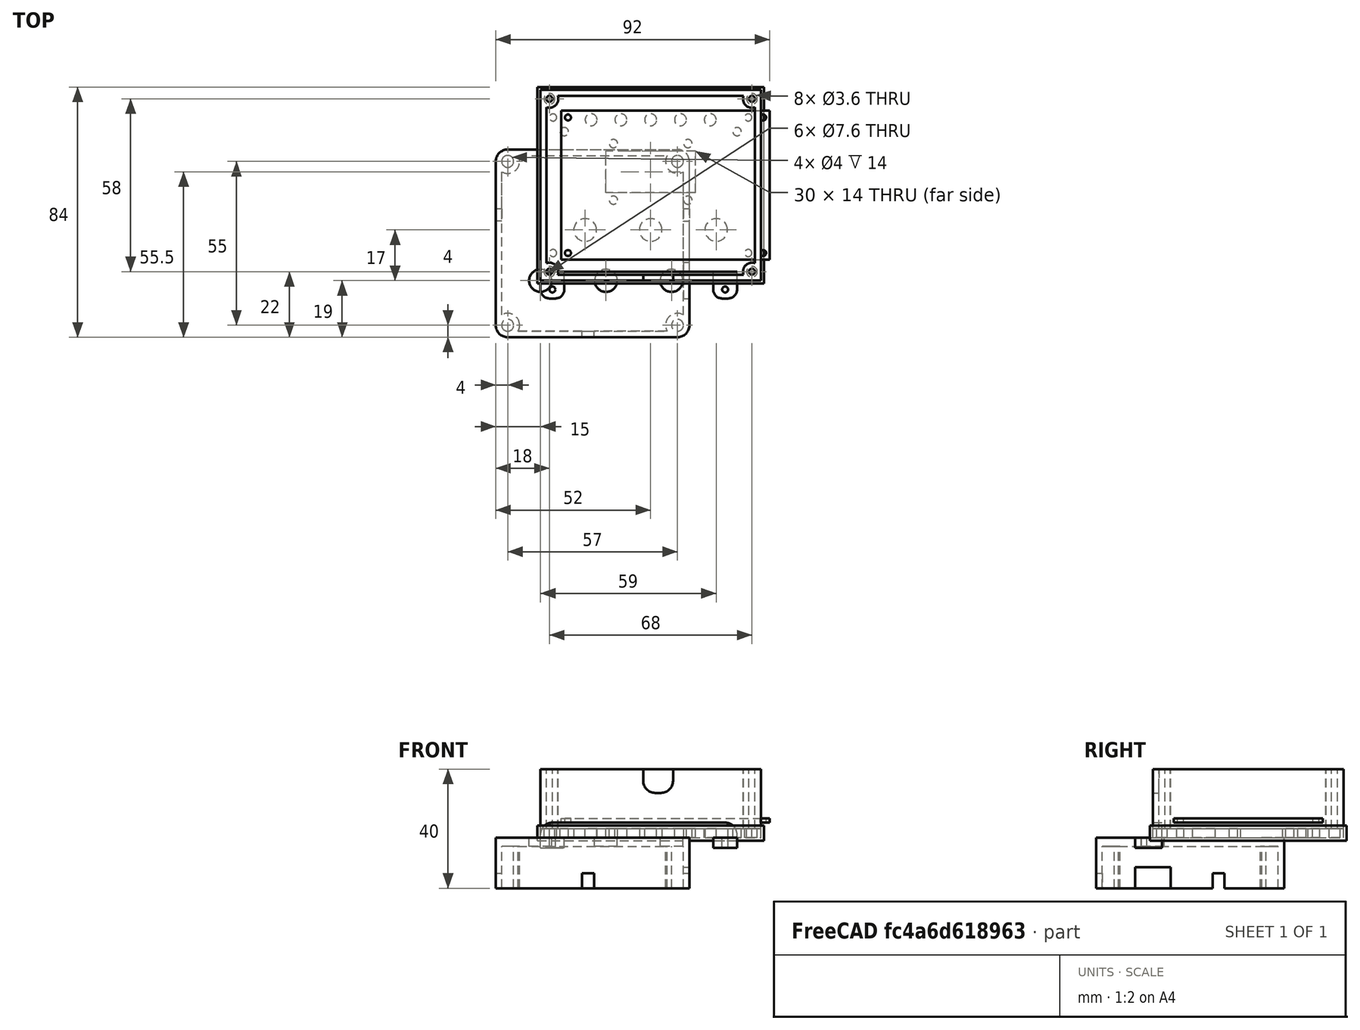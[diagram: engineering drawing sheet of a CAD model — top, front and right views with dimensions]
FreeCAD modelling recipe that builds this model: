
FCSTD DOCUMENT  (FreeCAD 0.18.4R)
Label: encoders
License: All rights reserved
LicenseURL: http://en.wikipedia.org/wiki/All_rights_reserved
objects: Part::Box×14, Part::Cylinder×13, Part::FeaturePython×13, Part::Cut×9, Part::MultiFuse×8, PartDesign::FeatureBase×5, PartDesign::Body×5, Part::Fillet×4, Path::FeaturePython×4, Part::Compound×1, Spreadsheet::Sheet×1, Part::Feature×1, App::FeaturePython×1, App::DocumentObjectGroup×1, Path::FeatureCompoundPython×1, App::Part×1
note: 74 computed .brp shape members not serialized (recipe doc carries the construction recipe); baked Part::Feature solids carry a one-line shape summary decoded from their .brp

FEATURE [Part::Box] Box  label="Cube"
  AttacherType = Attacher::AttachEngine3D
  Height = 17
  Length = 65
  Placement = pos=(-15,-19,-17) rot=(0,0,1;0rad)
  Width = 63
FEATURE [Part::Cylinder] Cylinder  label="encoder hole"
  Angle = 360
  AttacherType = Attacher::AttachEngine3D
  Height = 50
  Radius = 3.8
FEATURE [Part::Box] Box001  label="Cube001"
  AttacherType = Attacher::AttachEngine3D
  Height = 10
  Length = 12
  Placement = pos=(-6,-6,0) rot=(0,0,1;0rad)
  Width = 12
FEATURE [Part::Cylinder] Cylinder001  label="encoder cap"
  Angle = 360
  AttacherType = Attacher::AttachEngine3D
  Height = 15
  Placement = pos=(0,0,35) rot=(0,0,1;0rad)
  Radius = 10
FEATURE [Part::MultiFuse] Fusion  label="encoder fusion"
  Placement = pos=(0,0,-20) rot=(0,0,1;0rad)
  Shapes = -> [Box001,Cylinder,Cylinder001]
FEATURE [PartDesign::FeatureBase] Clone
  BaseFeature = -> Fusion
FEATURE [PartDesign::Body] Body  label="encoder clone"
  BaseFeature = -> Fusion
  Group = -> [Clone]
  Origin = -> Origin
  Placement = pos=(44,0,-20) rot=(0,0,1;0rad)
  Tip = -> Clone
FEATURE [PartDesign::FeatureBase] Clone001
  BaseFeature = -> Fusion
FEATURE [PartDesign::Body] Body001  label="encoder clone001"
  BaseFeature = -> Fusion
  Group = -> [Clone001]
  Origin = -> Origin001
  Placement = pos=(22,0,-20) rot=(0,0,1;0rad)
  Tip = -> Clone001
FEATURE [Part::Compound] Compound  label="encoder compound"
  Links = -> [Body,Body001,Fusion]
FEATURE [Part::Cylinder] Cylinder002  label="Cylinder"
  Angle = 360
  AttacherType = Attacher::AttachEngine3D
  Height = 17
  Placement = pos=(-11,-15,-17) rot=(0,0,1;0rad)
  Radius = 4
FEATURE [Part::FeaturePython] Array  # Draft array (typed FeaturePython)
  Angle = 360
  ArrayType = 0
  Axis = (0,0,1)
  Base = -> Cylinder002
  Center = (0,0,0)
  Fuse = false
  IntervalAxis = (0,0,0)
  IntervalX = (57,0,0)
  IntervalY = (0,55,0)
  IntervalZ = (0,0,1)
  NumberPolar = 1
  NumberX = 2
  NumberY = 2
  NumberZ = 1
FEATURE [Part::Cylinder] Cylinder003  label="Cylinder001"
  Angle = 360
  AttacherType = Attacher::AttachEngine3D
  Height = 17
  Placement = pos=(-11,-15,-20) rot=(0,0,1;0rad)
  Radius = 2
FEATURE [Part::FeaturePython] Array001  # Draft array (typed FeaturePython)
  Angle = 360
  ArrayType = 0
  Axis = (0,0,1)
  Base = -> Cylinder003
  Center = (0,0,0)
  Fuse = false
  IntervalAxis = (0,0,0)
  IntervalX = (57,0,0)
  IntervalY = (0,55,0)
  IntervalZ = (0,0,1)
  NumberPolar = 1
  NumberX = 2
  NumberY = 2
  NumberZ = 1
FEATURE [Part::Box] Box002  label="Cube002"
  AttacherType = Attacher::AttachEngine3D
  Height = 17
  Length = 61
  Placement = pos=(-13,-17,-20) rot=(0,0,1;0rad)
  Width = 59
FEATURE [Part::Cut] Cut001  label="box"
  Base = -> Box
  Tool = -> Box002
FEATURE [PartDesign::FeatureBase] Clone002
  BaseFeature = -> Compound
FEATURE [PartDesign::Body] Body002  label="encoder compound clone"
  BaseFeature = -> Compound
  Group = -> [Clone002]
  Origin = -> Origin002
  Tip = -> Clone002
FEATURE [Part::Fillet] Fillet
  Base = -> Cut001
  Edges = 4 edges r=4: [Edge1,Edge3,Edge6,Edge11]
FEATURE [Part::MultiFuse] Fusion001  label="body fusion"
  Shapes = -> [Array,Fillet]
FEATURE [Part::Box] Box003  label="Cube003"
  AttacherType = Attacher::AttachEngine3D
  Height = 10
  Length = 80
  Placement = pos=(-20,20,-22) rot=(0,0,1;0rad)
  Width = 4
FEATURE [Part::Box] Box004  label="Cube004"
  AttacherType = Attacher::AttachEngine3D
  Height = 10
  Length = 4
  Placement = pos=(14,-40,-22) rot=(0,0,1;0rad)
  Width = 40
FEATURE [Part::MultiFuse] Fusion002  label="encoder box extract"
  Shapes = -> [Array001,Body002,Box003,Box004]
FEATURE [Part::Cut] Cut  label="encoder box cut"
  Base = -> Fusion001
  Tool = -> Fusion002
FEATURE [Part::Box] Box005  label="pcb 7x5 mockup"
  AttacherType = Attacher::AttachEngine3D
  Height = 1.5
  Length = 70
  Width = 50
  expr: Width = p.pcb_width
  expr: Length = p.pcb_length
FEATURE [Part::Cylinder] Cylinder004  label="pcb hole"
  Angle = 360
  AttacherType = Attacher::AttachEngine3D
  Height = 10
  Radius = 1
FEATURE [Part::FeaturePython] Array002  label="pcb hole array"  # Draft array (typed FeaturePython)
  Angle = 360
  ArrayType = 0
  Axis = (0,0,1)
  Base = -> Cylinder004
  Center = (0,0,0)
  Fuse = false
  IntervalAxis = (0,0,0)
  IntervalX = (65.5,0,0)
  IntervalY = (0,45.5,0)
  IntervalZ = (0,0,1)
  NumberPolar = 1
  NumberX = 2
  NumberY = 2
  NumberZ = 1
  Placement = pos=(2.25,2.25,0) rot=(0,0,1;0rad)
  expr: IntervalY.y = p.pcb_hole_y_dist
  expr: IntervalX.x = p.pcb_hole_x_dist
  expr: Placement.Base.y = (p.pcb_width - p.pcb_hole_y_dist) / 2
  expr: Placement.Base.x = (p.pcb_length - p.pcb_hole_x_dist) / 2
FEATURE [Part::Cut] Cut002  label="pcb 7x5 mockup cut"
  Base = -> Box005
  Placement = pos=(7,7,5) rot=(0,0,1;0rad)
  Tool = -> Array002
FEATURE [Part::Box] Box006  label="bottom plate base"
  AttacherType = Attacher::AttachEngine3D
  Height = 3
  Length = 74
  Width = 64
  expr: Height = p.bottom_plate_height
  expr: Width = p.bottom_plate_width
  expr: Length = p.bottom_plate_length
FEATURE [Part::Cylinder] Cylinder005  label="pcb hole001"
  Angle = 360
  AttacherType = Attacher::AttachEngine3D
  Height = 10
  Radius = 1.2
FEATURE [Part::FeaturePython] Array003  label="pcb hole array001"  # Draft array (typed FeaturePython)
  Angle = 360
  ArrayType = 0
  Axis = (0,0,1)
  Base = -> Cylinder005
  Center = (0,0,0)
  Fuse = false
  IntervalAxis = (0,0,0)
  IntervalX = (65.5,0,0)
  IntervalY = (0,45.5,0)
  IntervalZ = (0,0,1)
  NumberPolar = 1
  NumberX = 2
  NumberY = 2
  NumberZ = 1
  Placement = pos=(4.25,9.25,-3) rot=(0,0,1;0rad)
  expr: IntervalY.y = p.pcb_hole_y_dist
  expr: IntervalX.x = p.pcb_hole_x_dist
  expr: Placement.Base.y = p.bottom_plate_pcb_hole_y_offset
  expr: Placement.Base.x = p.bottom_plate_pcb_hole_x_offset
FEATURE [Spreadsheet::Sheet] Spreadsheet  label="p"
  cells = A1=pcb_length; B1(pcb_length)=70; A2=pcb_width; B2(pcb_width)=50; A3=pcb_hole_x_dist; B3(pcb_hole_x_dist)=65.5; A4=pcb_hole_y_dist; B4(pcb_hole_y_dist)=45.5; A5=bottom_plate_height; B5(bottom_plate_height)=3; A6=bottom_plate_length; B6(bottom_plate_length)=74; A7=bottom_plate_width; B7(bottom_plate_width)=64; A8=bottom_plate_pcb_hole_x_offset; B8(bottom_plate_pcb_hole_x_offset)==(p.bottom_plate_length - p.pcb_hole_x_dist) / 2; A9=bottom_plate_pcb_hole_y_offset; B9(bottom_plate_pcb_hole_y_offset)==(p.bottom_plate_width - p.pcb_hole_y_dist) / 2; A10=box_wall; B10(box_wall)=2; A11=box_wall_height; B11(box_wall_height)=20; A12=box_wall_hole_r; B12(box_wall_hole_r)=1; A13=button_hole_r; B13(button_hole_r)=2; A14=tft_hole_length; B14(tft_hole_length)=30; A15=tft_hole_width; B15(tft_hole_width)=14; A16=tft_bolt_hole_dist_x; B16(tft_bolt_hole_dist_x)=25; A17=tft_bolt_hole_dist_y; B17(tft_bolt_hole_dist_y)=19; A19=
FEATURE [Part::Box] Box007  label="wall outer box"
  AttacherType = Attacher::AttachEngine3D
  Height = 20
  Length = 74
  Width = 64
  expr: Height = p.box_wall_height
  expr: Width = p.bottom_plate_width
  expr: Length = p.bottom_plate_length
FEATURE [Part::Box] Box008  label="wall inner extraction"
  AttacherType = Attacher::AttachEngine3D
  Height = 20
  Length = 70
  Placement = pos=(2,2,0) rot=(0,0,1;0rad)
  Width = 60
  expr: Height = p.box_wall_height
  expr: Placement.Base.y = p.box_wall
  expr: Placement.Base.x = p.box_wall
  expr: Width = p.bottom_plate_width - 2 * p.box_wall
  expr: Length = p.bottom_plate_length - 2 * p.box_wall
FEATURE [Part::Cut] Cut004  label="wall box cut"
  Base = -> Box007
  Tool = -> Box008
FEATURE [Part::Cylinder] Cylinder006  label="wall box hole body"
  Angle = 360
  AttacherType = Attacher::AttachEngine3D
  Height = 20
  Radius = 3
  expr: Radius = p.box_wall_hole_r + p.box_wall
  expr: Height = p.box_wall_height
FEATURE [Part::Cylinder] Cylinder007  label="wall box hole"
  Angle = 360
  AttacherType = Attacher::AttachEngine3D
  Height = 20
  Radius = 1
  expr: Radius = p.box_wall_hole_r
  expr: Height = p.box_wall_height
FEATURE [Part::Cut] Cut005  label="wall box hole stand"
  Base = -> Cylinder006
  Placement = pos=(3,3,0) rot=(0,0,1;0rad)
  Tool = -> Cylinder007
  expr: Placement.Base.y = p.box_wall + p.box_wall_hole_r
  expr: Placement.Base.x = p.box_wall + p.box_wall_hole_r
FEATURE [Part::FeaturePython] Array004  label="wall box hole stand array"  # Draft array (typed FeaturePython)
  Angle = 360
  ArrayType = 0
  Axis = (0,0,1)
  Base = -> Cut005
  Center = (0,0,0)
  Fuse = false
  IntervalAxis = (0,0,0)
  IntervalX = (68,0,0)
  IntervalY = (0,58,0)
  IntervalZ = (0,0,1)
  NumberPolar = 1
  NumberX = 2
  NumberY = 2
  NumberZ = 1
  expr: IntervalY.y = p.bottom_plate_width - 2 * (p.box_wall + p.box_wall_hole_r)
  expr: IntervalX.x = p.bottom_plate_length - 2 * (p.box_wall + p.box_wall_hole_r)
FEATURE [Part::MultiFuse] Fusion003  label="wall fusion"
  Placement = pos=(0,0,3) rot=(0,0,1;0rad)
  Shapes = -> [Array004,Cut004]
  expr: Placement.Base.z = p.bottom_plate_height
FEATURE [Part::Cylinder] Cylinder009  label="wall box hole through"
  Angle = 360
  AttacherType = Attacher::AttachEngine3D
  Height = 20
  Placement = pos=(3,3,0) rot=(0,0,1;0rad)
  Radius = 1.8
  expr: Placement.Base.y = p.box_wall + p.box_wall_hole_r
  expr: Placement.Base.x = p.box_wall + p.box_wall_hole_r
FEATURE [Part::FeaturePython] Array005  label="wall box hole stand array001"  # Draft array (typed FeaturePython)
  Angle = 360
  ArrayType = 0
  Axis = (0,0,1)
  Base = -> Cylinder009
  Center = (0,0,0)
  Fuse = false
  IntervalAxis = (0,0,0)
  IntervalX = (68,0,0)
  IntervalY = (0,58,0)
  IntervalZ = (0,0,1)
  NumberPolar = 1
  NumberX = 2
  NumberY = 2
  NumberZ = 1
  expr: IntervalY.y = p.bottom_plate_width - 2 * (p.box_wall + p.box_wall_hole_r)
  expr: IntervalX.x = p.bottom_plate_length - 2 * (p.box_wall + p.box_wall_hole_r)
FEATURE [Part::MultiFuse] Fusion004  label="bottom plate hole fusion"
  Shapes = -> [Array003,Array005]
FEATURE [Part::Cut] Cut003  label="bottom plate cut"
  Base = -> Box006
  Tool = -> Fusion004
FEATURE [Part::Box] Box009  label="top plate base"
  AttacherType = Attacher::AttachEngine3D
  Height = 3
  Length = 74
  Width = 64
  expr: Height = p.bottom_plate_height
  expr: Width = p.bottom_plate_width
  expr: Length = p.bottom_plate_length
FEATURE [Part::Cylinder] Cylinder011  label="wall box hole through001"
  Angle = 360
  AttacherType = Attacher::AttachEngine3D
  Height = 20
  Placement = pos=(3,3,0) rot=(0,0,1;0rad)
  Radius = 1.8
  expr: Placement.Base.y = p.box_wall + p.box_wall_hole_r
  expr: Placement.Base.x = p.box_wall + p.box_wall_hole_r
FEATURE [Part::FeaturePython] Array007  label="wall box hole stand array002"  # Draft array (typed FeaturePython)
  Angle = 360
  ArrayType = 0
  Axis = (0,0,1)
  Base = -> Cylinder011
  Center = (0,0,0)
  Fuse = false
  IntervalAxis = (0,0,0)
  IntervalX = (68,0,0)
  IntervalY = (0,58,0)
  IntervalZ = (0,0,1)
  NumberPolar = 1
  NumberX = 2
  NumberY = 2
  NumberZ = 1
  expr: IntervalY.y = p.bottom_plate_width - 2 * (p.box_wall + p.box_wall_hole_r)
  expr: IntervalX.x = p.bottom_plate_length - 2 * (p.box_wall + p.box_wall_hole_r)
FEATURE [PartDesign::FeatureBase] Clone003
  BaseFeature = -> Compound
FEATURE [PartDesign::Body] Body003  label="encoder compound clone001"
  BaseFeature = -> Compound
  Group = -> [Clone003]
  Origin = -> Origin003
  Placement = pos=(59,17,-2) rot=(0,1,0;3.14159rad)
  Tip = -> Clone003
FEATURE [Part::Box] Box010  label="wall fusion wire hole"
  AttacherType = Attacher::AttachEngine3D
  Height = 10
  Length = 10
  Placement = pos=(34.5,-4.5,15) rot=(0,0,1;0rad)
  Width = 10
FEATURE [Part::Fillet] Fillet001
  Base = -> Box010
  Edges = 2 edges r=4: [Edge4,Edge8]
FEATURE [Part::Cut] Cut007  label="wall fusion cut"
  Base = -> Fusion003
  Tool = -> Fillet001
FEATURE [Part::Cylinder] Cylinder012  label="button hole"
  Angle = 360
  AttacherType = Attacher::AttachEngine3D
  Height = 20
  Radius = 2
  expr: Radius = p.button_hole_r
FEATURE [Part::FeaturePython] Array008  label="button hole array"  # Draft array (typed FeaturePython)
  Angle = 360
  ArrayType = 0
  Axis = (0,0,1)
  Base = -> Cylinder012
  Center = (0,0,0)
  Fuse = false
  IntervalAxis = (0,0,0)
  IntervalX = (10,0,0)
  IntervalY = (0,1,0)
  IntervalZ = (0,0,1)
  NumberPolar = 1
  NumberX = 5
  NumberY = 1
  NumberZ = 1
  Placement = pos=(17,54,-9) rot=(0,0,1;0rad)
FEATURE [Part::Cylinder] Cylinder013  label="m2.5 bolt hole"
  Angle = 360
  AttacherType = Attacher::AttachEngine3D
  Height = 20
  Radius = 1.4
FEATURE [Part::FeaturePython] Array009  label="m2.5 bolt hole array"  # Draft array (typed FeaturePython)
  Angle = 360
  ArrayType = 0
  Axis = (0,0,1)
  Base = -> Cylinder013
  Center = (0,0,0)
  Fuse = false
  IntervalAxis = (0,0,0)
  IntervalX = (58,0,0)
  IntervalY = (0,1,0)
  IntervalZ = (0,0,1)
  NumberPolar = 1
  NumberX = 2
  NumberY = 1
  NumberZ = 1
  Placement = pos=(8,50,-8) rot=(0,0,1;0rad)
FEATURE [PartDesign::FeatureBase] Clone004
  BaseFeature = -> Cylinder013
FEATURE [PartDesign::Body] Body004  label="m2.5 bolt hole clone"
  BaseFeature = -> Cylinder013
  Group = -> [Clone004]
  Origin = -> Origin004
  Tip = -> Clone004
FEATURE [Part::FeaturePython] Array010  label="m2.5 bolt hole array001"  # Draft array (typed FeaturePython)
  Angle = 360
  ArrayType = 0
  Axis = (0,0,1)
  Base = -> Body004
  Center = (0,0,0)
  Fuse = false
  IntervalAxis = (0,0,0)
  IntervalX = (25,0,0)
  IntervalY = (0,19,0)
  IntervalZ = (0,0,1)
  NumberPolar = 1
  NumberX = 2
  NumberY = 2
  NumberZ = 1
  expr: IntervalX.x = p.tft_bolt_hole_dist_x
  expr: IntervalY.y = p.tft_bolt_hole_dist_y
FEATURE [Part::Box] Box011  label="tft hole cube"
  AttacherType = Attacher::AttachEngine3D
  Height = 20
  Length = 30
  Placement = pos=(-2.5,2.5,0) rot=(0,0,1;0rad)
  Width = 14
  expr: Placement.Base.y = (p.tft_bolt_hole_dist_y - p.tft_hole_width) / 2
  expr: Placement.Base.x = (p.tft_bolt_hole_dist_x - p.tft_hole_length) / 2
  expr: Length = p.tft_hole_length
  expr: Width = p.tft_hole_width
FEATURE [Part::MultiFuse] Fusion006  label="tft hole fusion"
  Placement = pos=(24.5,27,-5) rot=(0,0,1;0rad)
  Shapes = -> [Box011,Array010]
FEATURE [Part::MultiFuse] Fusion005  label="bottom plate hole fusion001"
  Shapes = -> [Array007,Body003,Array008,Array009,Fusion006]
FEATURE [Part::Cut] Cut006  label="top plate cut"
  Base = -> Box009
  Tool = -> Fusion005
FEATURE [Part::Feature] Cut006_solid  label="top plate cut (Solid)"
  shape: bbox 74 x 64 x 3 mm, 28 faces (baked)
FEATURE [App::FeaturePython] SetupSheet  # Path/CAM operation (typed FeaturePython)
  ClearanceHeightExpression = OpStockZMax+SetupSheet.ClearanceHeightOffset
  ClearanceHeightOffset = 0
  FinalDepthExpression = OpFinalDepth
  HorizRapid = 100
  SafeHeightExpression = OpStockZMax+SetupSheet.SafeHeightOffset
  SafeHeightOffset = 0
  StartDepthExpression = OpStartDepth
  StepDownExpression = OpToolDiameter
  VertRapid = 100
FEATURE [Part::FeaturePython] Clone005  label="Model-top plate cut (Solid)"  # Draft clone (typed FeaturePython)
  AttacherType = Attacher::AttachEngine3D
  Fuse = false
  Objects = -> [Cut006_solid]
  PathResource = Model
  Scale = (1,1,1)
FEATURE [App::DocumentObjectGroup] Model
  Group = -> [Clone005]
FEATURE [Path::FeaturePython] T3__laser  label="T3: laser"  # Path/CAM operation (typed FeaturePython)
  HorizFeed = 0.5
  HorizRapid = 100
  SpindleDir = 0
  SpindleSpeed = 1000
  ToolNumber = 3
  VertFeed = 0.5
  VertRapid = 100
  expr: VertRapid = SetupSheet.VertRapid
  expr: HorizRapid = SetupSheet.HorizRapid
FEATURE [Part::FeaturePython] Stock  # WARN: FeaturePython — macro-defined, semantics opaque (R4)
  Base = -> Model
  ExtXneg = 1
  ExtXpos = 1
  ExtYneg = 1
  ExtYpos = 1
  ExtZneg = 1
  ExtZpos = 1
  StockType = FromBase
FEATURE [Path::FeaturePython] Engrave  # Path/CAM operation (typed FeaturePython)
  Active = true
  Base = -> [Clone005]
  ClearanceHeight = 0.2
  FinalDepth = 0
  OpFinalDepth = 2.8
  OpStartDepth = 3
  OpStockZMax = 4
  OpStockZMin = -1
  OpToolDiameter = 0.2
  SafeHeight = 0.2
  StartDepth = 0.1
  StartVertex = 0
  StepDown = 0.2
  ToolController = -> T3__laser
  expr: StepDown = OpToolDiameter
FEATURE [Path::FeaturePython] Contour  # Path/CAM operation (typed FeaturePython)
  Active = true
  AreaParams:
    Tolerance = 1e-07
    FitArcs = True
    Simplify = False
    CleanDistance = 0.0
    Accuracy = 0.01
    Unit = 1.0
    MinArcPoints = 4
    MaxArcPoints = 100
    ClipperScale = 10000000.0
    Fill = 0
    Coplanar = 2
    Reorient = True
    Outline = False
    Explode = False
    OpenMode = 0
    Deflection = 0.01
    SubjectFill = 0
    ClipFill = 0
    Offset = 0.1
    ExtraPass = 0
    Stepover = 0.0
    LastStepover = 0.0
    JoinType = 0
    EndType = 0
    MiterLimit = 2.0
    RoundPrecision = 0.0
    PocketMode = 0
    ToolRadius = 1.0
    PocketExtraOffset = 0.0
    PocketStepover = 0.0
    PocketLastStepover = 0.0
    FromCenter = False
    Angle = 45.0
    AngleShift = 0.0
    Shift = 0.0
    Thicken = False
    SectionCount = -1
    Stepdown = 1.0
    SectionOffset = 0.0
    SectionTolerance = 1e-06
    SectionMode = 2
    Project = False
  ClearanceHeight = 0.1
  Direction = 0
  FinalDepth = 0
  JoinType = 0
  MiterLimit = 0.1
  OffsetExtra = 0
  OpFinalDepth = -1
  OpStartDepth = 4
  OpStockZMax = 4
  OpStockZMin = -1
  OpToolDiameter = 0.2
  PathParams = {'orientation': 1, 'feedrate': 0.5, 'feedrate_v': 0.5, 'verbose': True, 'resume_height': 0.1, 'retraction': 0.1, 'return_end': True, 'preamble': False}
  SafeHeight = 0.1
  Side = 0
  StartDepth = 0.1
  StartPoint = (0,0,0)
  StepDown = 0.2
  ToolController = -> T3__laser
  UseComp = true
  UseStartPoint = false
  expr: StepDown = OpToolDiameter
FEATURE [Path::FeatureCompoundPython] Operations  # Path/CAM operation (typed FeaturePython)
  Group = -> [Engrave,Contour]
  UsePlacements = false
FEATURE [Path::FeaturePython] Job  label="encoders Job"  # Path/CAM operation (typed FeaturePython)
  GeometryTolerance = 0.01
  Model = -> Model
  Operations = -> Operations
  PostProcessor = 1
  PostProcessorOutputFile = <userpath>/work/roborep/freecad/microscope/encoders.gcode
  SetupSheet = -> SetupSheet
  Stock = -> Stock
  ToolController = -> [T3__laser]
FEATURE [Part::Box] Box012  label="long cube"
  AttacherType = Attacher::AttachEngine3D
  Height = 5
  Length = 66
  Width = 3
FEATURE [Part::Box] Box013  label="Cube005"
  AttacherType = Attacher::AttachEngine3D
  Height = 3.5
  Length = 8
  Placement = pos=(0,0,-3.5) rot=(0,0,1;0rad)
  Width = 9
FEATURE [Part::Cylinder] Cylinder014  label="Cylinder002"
  Angle = 360
  AttacherType = Attacher::AttachEngine3D
  Height = 10
  Placement = pos=(4,3,-5) rot=(0,0,1;0rad)
  Radius = 1
FEATURE [Part::Fillet] Fillet002
  Base = -> Box013
  Edges = 2 edges r=3: [Edge1,Edge5]
FEATURE [Part::Cut] Cut008
  Base = -> Fillet002
  Tool = -> Cylinder014
FEATURE [Part::FeaturePython] Array011  # Draft array (typed FeaturePython)
  Angle = 360
  ArrayType = 0
  Axis = (0,0,1)
  Base = -> Cut008
  Center = (0,0,0)
  Fuse = false
  IntervalAxis = (0,0,0)
  IntervalX = (58,0,0)
  IntervalY = (0,1,0)
  IntervalZ = (0,0,1)
  NumberPolar = 1
  NumberX = 2
  NumberY = 1
  NumberZ = 1
  Placement = pos=(0,-6,0) rot=(0,0,1;0rad)
FEATURE [Part::Fillet] Fillet003  label="long cube fillet"
  Base = -> Box012
  Edges = 2 edges r=4: [Edge2,Edge6]
FEATURE [Part::MultiFuse] Fusion007  label="botton holder fusion"
  Shapes = -> [Array011,Fillet003]
FEATURE [App::Part] Part  label="button holder part"
  Group = -> [Box012,Box013,Array011,Cut008,Cylinder014,Fillet002,Fusion007]
  Origin = -> Origin005
  Placement = pos=(4,53,6.5) rot=(0,0,1;0rad)
